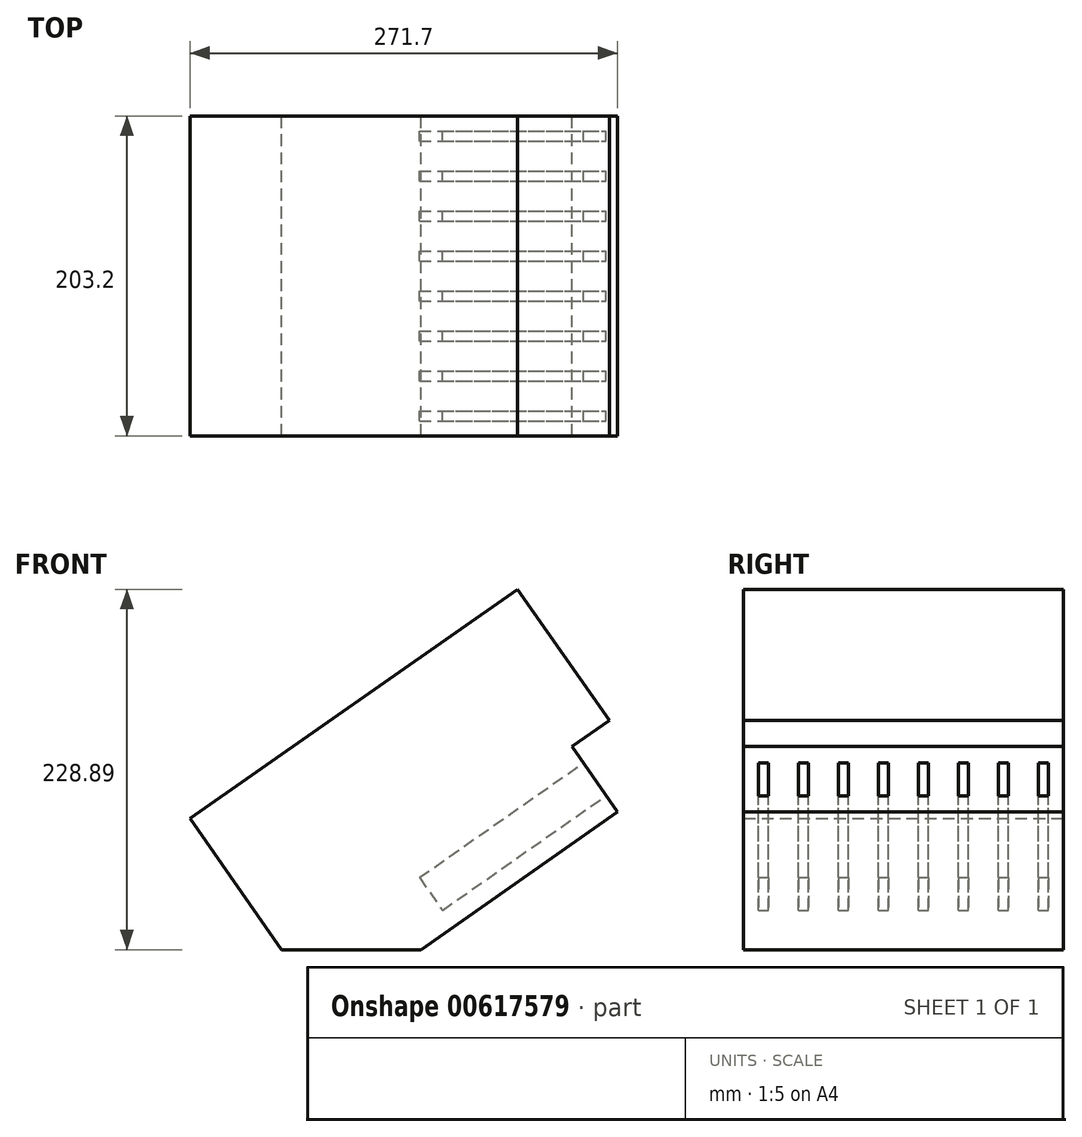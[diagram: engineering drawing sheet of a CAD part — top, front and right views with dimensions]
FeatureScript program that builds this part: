
annotation { "Feature Type Name" : "Feature", "Feature Type Description" : "" }
export const myFeature = defineFeature(function(context is Context, id is Id, definition is map)
    precondition{}
    {
        {
            var Q0;
            Q0=qCreatedBy(makeId("Front.planeOp"),FACE);
            var sketch = newSketch(context, id + "F0", { "sketchPlane" : qUnion([Q0])});
            skLineSegment(sketch, "E0", {"start": v(-169.07, -25.65) * mm, "end": v(39.02, 120.01) * mm});
            skLineSegment(sketch, "E1", {"start": v(39.02, 120.01) * mm, "end": v(97.28, 36.78) * mm});
            skLineSegment(sketch, "E2", {"start": v(97.28, 36.78) * mm, "end": v(-110.8, -108.88) * mm});
            skLineSegment(sketch, "E3", {"start": v(-110.8, -108.88) * mm, "end": v(-169.07, -25.65) * mm});
            skLineSegment(sketch, "E4", {"start": v(-110.8, -108.88) * mm, "end": v(-22.22, -108.88) * mm});
            skLineSegment(sketch, "E5", {"start": v(-22.22, -108.88) * mm, "end": v(102.63, -21.48) * mm});
            skLineSegment(sketch, "E6", {"start": v(102.63, -21.48) * mm, "end": v(73.5, 20.13) * mm});
            skSolve(sketch);
        }
        {
            var Q0;
            Q0 = qSketchRegion(id + "F0", true);
            extrude(context, id + "F1", {"entities" : qUnion([Q0]), "depth" : 203.2 * mm, "offsetDistance" : 25.4 * mm});
        }
        {
            var Q0;
            Q0=makeQuery(id+"F1.opExtrude","SWEPT_FACE",FACE,{"disambiguationData":[OSD([sQuery(id+"F0.wireOp",EDGE,"E6")])]});
            var sketch = newSketch(context, id + "F2", { "sketchPlane" : qUnion([Q0])});
            skLineSegment(sketch, "E7.bottom", {"start": v(-193.68, -38.35) * mm, "end": v(-187.33, -38.35) * mm});
            skLineSegment(sketch, "E7.top", {"start": v(-193.68, -63.75) * mm, "end": v(-187.33, -63.75) * mm});
            skLineSegment(sketch, "E7.left", {"start": v(-193.68, -38.35) * mm, "end": v(-193.68, -63.75) * mm});
            skLineSegment(sketch, "E7.right", {"start": v(-187.33, -38.35) * mm, "end": v(-187.33, -63.75) * mm});
            skLineSegment(sketch, "E8.1.0.0", {"start": v(-161.93, -38.35) * mm, "end": v(-161.93, -63.75) * mm});
            skLineSegment(sketch, "E8.1.0.1", {"start": v(-168.28, -38.35) * mm, "end": v(-168.28, -63.75) * mm});
            skLineSegment(sketch, "E8.1.0.2", {"start": v(-168.28, -38.35) * mm, "end": v(-161.93, -38.35) * mm});
            skLineSegment(sketch, "E8.1.0.3", {"start": v(-168.28, -63.75) * mm, "end": v(-161.93, -63.75) * mm});
            skLineSegment(sketch, "E8.2.0.0", {"start": v(-136.53, -38.35) * mm, "end": v(-136.53, -63.75) * mm});
            skLineSegment(sketch, "E8.2.0.1", {"start": v(-142.88, -38.35) * mm, "end": v(-142.88, -63.75) * mm});
            skLineSegment(sketch, "E8.2.0.2", {"start": v(-142.88, -38.35) * mm, "end": v(-136.53, -38.35) * mm});
            skLineSegment(sketch, "E8.2.0.3", {"start": v(-142.88, -63.75) * mm, "end": v(-136.53, -63.75) * mm});
            skLineSegment(sketch, "E8.3.0.0", {"start": v(-111.12, -38.35) * mm, "end": v(-111.12, -63.75) * mm});
            skLineSegment(sketch, "E8.3.0.1", {"start": v(-117.47, -38.35) * mm, "end": v(-117.47, -63.75) * mm});
            skLineSegment(sketch, "E8.3.0.2", {"start": v(-117.47, -38.35) * mm, "end": v(-111.12, -38.35) * mm});
            skLineSegment(sketch, "E8.3.0.3", {"start": v(-117.47, -63.75) * mm, "end": v(-111.12, -63.75) * mm});
            skLineSegment(sketch, "E8.4.0.0", {"start": v(-85.72, -38.35) * mm, "end": v(-85.72, -63.75) * mm});
            skLineSegment(sketch, "E8.4.0.1", {"start": v(-92.07, -38.35) * mm, "end": v(-92.07, -63.75) * mm});
            skLineSegment(sketch, "E8.4.0.2", {"start": v(-92.07, -38.35) * mm, "end": v(-85.72, -38.35) * mm});
            skLineSegment(sketch, "E8.4.0.3", {"start": v(-92.07, -63.75) * mm, "end": v(-85.72, -63.75) * mm});
            skLineSegment(sketch, "E8.5.0.0", {"start": v(-60.32, -38.35) * mm, "end": v(-60.32, -63.75) * mm});
            skLineSegment(sketch, "E8.5.0.1", {"start": v(-66.67, -38.35) * mm, "end": v(-66.67, -63.75) * mm});
            skLineSegment(sketch, "E8.5.0.2", {"start": v(-66.67, -38.35) * mm, "end": v(-60.32, -38.35) * mm});
            skLineSegment(sketch, "E8.5.0.3", {"start": v(-66.67, -63.75) * mm, "end": v(-60.32, -63.75) * mm});
            skLineSegment(sketch, "E8.6.0.0", {"start": v(-34.92, -38.35) * mm, "end": v(-34.92, -63.75) * mm});
            skLineSegment(sketch, "E8.6.0.1", {"start": v(-41.27, -38.35) * mm, "end": v(-41.27, -63.75) * mm});
            skLineSegment(sketch, "E8.6.0.2", {"start": v(-41.27, -38.35) * mm, "end": v(-34.92, -38.35) * mm});
            skLineSegment(sketch, "E8.6.0.3", {"start": v(-41.27, -63.75) * mm, "end": v(-34.92, -63.75) * mm});
            skLineSegment(sketch, "E8.7.0.0", {"start": v(-9.52, -38.35) * mm, "end": v(-9.52, -63.75) * mm});
            skLineSegment(sketch, "E8.7.0.1", {"start": v(-15.87, -38.35) * mm, "end": v(-15.87, -63.75) * mm});
            skLineSegment(sketch, "E8.7.0.2", {"start": v(-15.87, -38.35) * mm, "end": v(-9.52, -38.35) * mm});
            skLineSegment(sketch, "E8.7.0.3", {"start": v(-15.87, -63.75) * mm, "end": v(-9.52, -63.75) * mm});
            skLineSegment(sketch, "E8.direction1", {"start": v(-187.33, -63.75) * mm, "end": v(-161.93, -63.75) * mm, "construction": true});
            skSolve(sketch);
        }
        {
            var Q0;
            Q0 = qSketchRegion(id + "F2", true);
            extrude(context, id + "F3", {"entities" : qUnion([Q0]), "operationType" : NewBodyOperationType.REMOVE, "oppositeDirection" : true, "depth" : 127 * mm, "offsetDistance" : 25.4 * mm});
        }
    });
